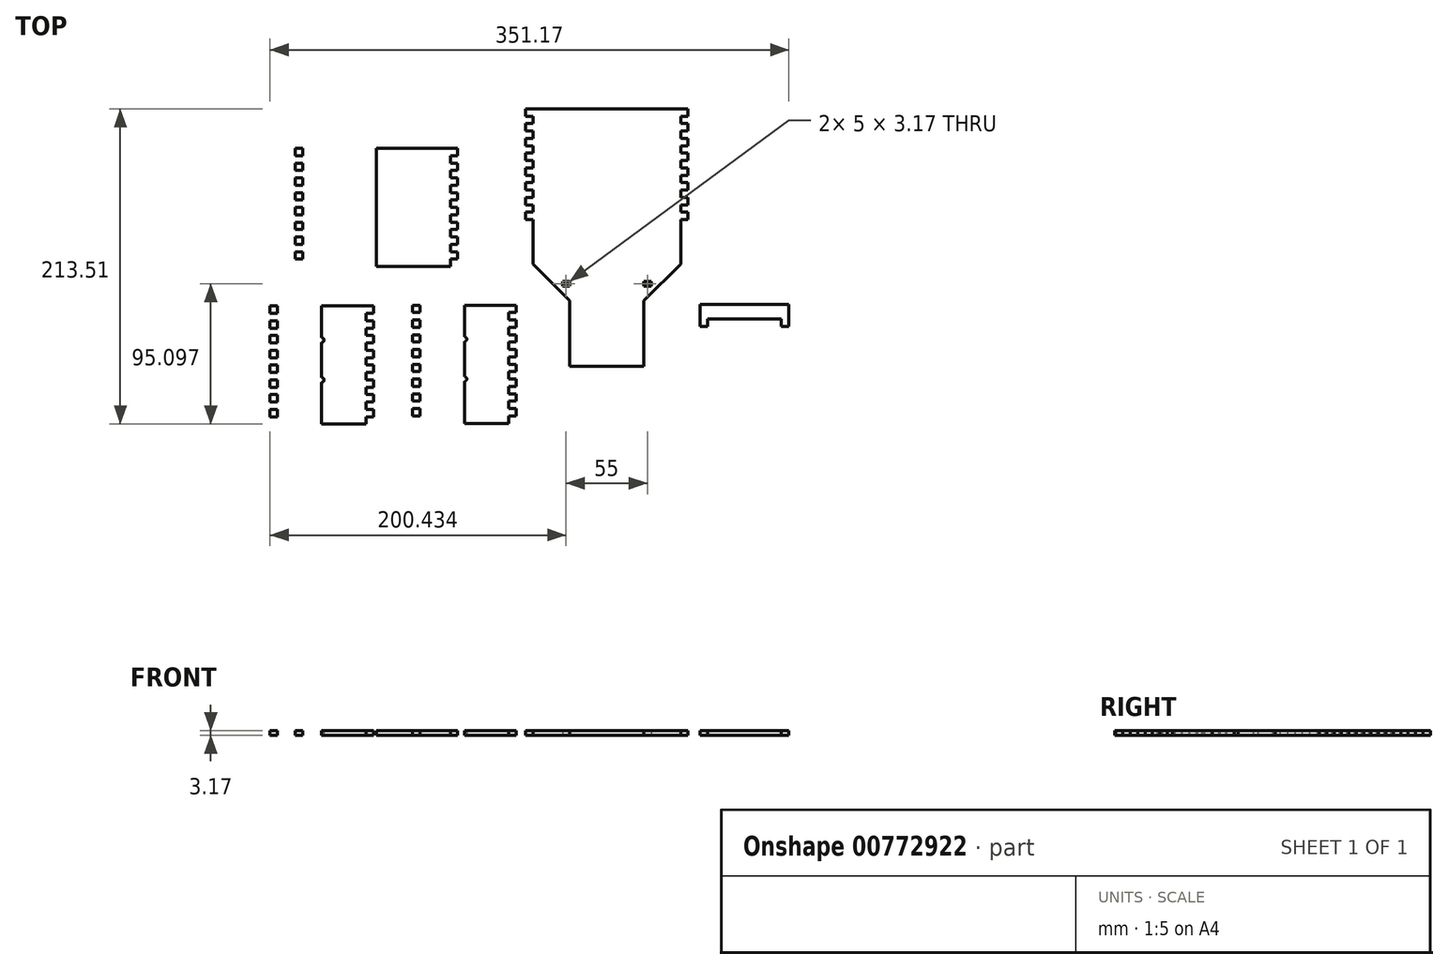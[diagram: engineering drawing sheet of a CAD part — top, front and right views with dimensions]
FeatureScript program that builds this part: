
annotation { "Feature Type Name" : "Feature", "Feature Type Description" : "" }
export const myFeature = defineFeature(function(context is Context, id is Id, definition is map)
    precondition{}
    {
        {
            var Q0;
            Q0=qCreatedBy(makeId("Top.planeOp"),FACE);
            var sketch = newSketch(context, id + "F0", { "sketchPlane" : qUnion([Q0])});
            skLineSegment(sketch, "E0", {"start": v(-34.3, 0) * mm, "end": v(-34.3, 80) * mm});
            skLineSegment(sketch, "E1.bottom", {"start": v(-34.3, 80) * mm, "end": v(-39.3, 80) * mm});
            skLineSegment(sketch, "E1.top", {"start": v(-34.3, 75) * mm, "end": v(-39.3, 75) * mm});
            skLineSegment(sketch, "E1.left", {"start": v(-34.3, 80) * mm, "end": v(-34.3, 75) * mm});
            skLineSegment(sketch, "E1.right", {"start": v(-39.3, 80) * mm, "end": v(-39.3, 75) * mm});
            skLineSegment(sketch, "E2.MirrorCS", {"start": v(-34.3, 70) * mm, "end": v(-39.3, 70) * mm});
            skLineSegment(sketch, "E3.MirrorCS", {"start": v(-34.3, 65) * mm, "end": v(-39.3, 65) * mm});
            skLineSegment(sketch, "E4.MirrorCS", {"start": v(-34.3, 60) * mm, "end": v(-39.3, 60) * mm});
            skLineSegment(sketch, "E5.MirrorCS", {"start": v(-34.3, 55) * mm, "end": v(-39.3, 55) * mm});
            skLineSegment(sketch, "E6.MirrorCS", {"start": v(-34.3, 50) * mm, "end": v(-39.3, 50) * mm});
            skLineSegment(sketch, "E7.MirrorCS", {"start": v(-34.3, 45) * mm, "end": v(-39.3, 45) * mm});
            skLineSegment(sketch, "E8.MirrorCS", {"start": v(-34.3, 40) * mm, "end": v(-39.3, 40) * mm});
            skLineSegment(sketch, "E9.MirrorCS", {"start": v(-34.3, 35) * mm, "end": v(-39.3, 35) * mm});
            skLineSegment(sketch, "E10.MirrorCS", {"start": v(-34.3, 30) * mm, "end": v(-39.3, 30) * mm});
            skLineSegment(sketch, "E11.MirrorCS", {"start": v(-34.3, 25) * mm, "end": v(-39.3, 25) * mm});
            skLineSegment(sketch, "E12.MirrorCS", {"start": v(-34.3, 20) * mm, "end": v(-39.3, 20) * mm});
            skLineSegment(sketch, "E13.MirrorCS", {"start": v(-34.3, 15) * mm, "end": v(-39.3, 15) * mm});
            skLineSegment(sketch, "E14.MirrorCS", {"start": v(-34.3, 10) * mm, "end": v(-39.3, 10) * mm});
            skLineSegment(sketch, "E15.MirrorCS", {"start": v(-34.3, 5) * mm, "end": v(-39.3, 5) * mm});
            skLineSegment(sketch, "E16", {"start": v(-34.3, 80) * mm, "end": v(15.7, 80) * mm});
            skLineSegment(sketch, "E17", {"start": v(15.7, 80) * mm, "end": v(15.7, 0) * mm});
            skLineSegment(sketch, "E18", {"start": v(15.7, 0) * mm, "end": v(-34.3, 0) * mm});
            skLineSegment(sketch, "E19", {"start": v(-39.3, 70) * mm, "end": v(-39.3, 65) * mm});
            skLineSegment(sketch, "E20", {"start": v(-39.3, 60) * mm, "end": v(-39.3, 55) * mm});
            skLineSegment(sketch, "E21", {"start": v(-39.3, 50) * mm, "end": v(-39.3, 45) * mm});
            skLineSegment(sketch, "E22", {"start": v(-39.3, 40) * mm, "end": v(-39.3, 35) * mm});
            skLineSegment(sketch, "E23", {"start": v(-39.3, 30) * mm, "end": v(-39.3, 25) * mm});
            skLineSegment(sketch, "E24", {"start": v(-39.3, 20) * mm, "end": v(-39.3, 15) * mm});
            skLineSegment(sketch, "E25", {"start": v(-39.3, 10) * mm, "end": v(-39.3, 5) * mm});
            skLineSegment(sketch, "E26.MirrorCS", {"start": v(65.7, 80) * mm, "end": v(65.7, 75) * mm});
            skLineSegment(sketch, "E27.MirrorCS", {"start": v(65.7, 45) * mm, "end": v(70.7, 45) * mm});
            skLineSegment(sketch, "E28.MirrorCS", {"start": v(65.7, 60) * mm, "end": v(70.7, 60) * mm});
            skLineSegment(sketch, "E29.MirrorCS", {"start": v(65.7, 0) * mm, "end": v(65.7, 80) * mm});
            skLineSegment(sketch, "E30.MirrorCS", {"start": v(70.7, 40) * mm, "end": v(70.7, 35) * mm});
            skLineSegment(sketch, "E31.MirrorCS", {"start": v(65.7, 80) * mm, "end": v(70.7, 80) * mm});
            skLineSegment(sketch, "E32.MirrorCS", {"start": v(65.7, 65) * mm, "end": v(70.7, 65) * mm});
            skLineSegment(sketch, "E33.MirrorCS", {"start": v(65.7, 5) * mm, "end": v(70.7, 5) * mm});
            skLineSegment(sketch, "E34.MirrorCS", {"start": v(65.7, 40) * mm, "end": v(70.7, 40) * mm});
            skLineSegment(sketch, "E35.MirrorCS", {"start": v(65.7, 50) * mm, "end": v(70.7, 50) * mm});
            skLineSegment(sketch, "E36.MirrorCS", {"start": v(70.7, 80) * mm, "end": v(70.7, 75) * mm});
            skLineSegment(sketch, "E37.MirrorCS", {"start": v(65.7, 70) * mm, "end": v(70.7, 70) * mm});
            skLineSegment(sketch, "E38.MirrorCS", {"start": v(70.7, 10) * mm, "end": v(70.7, 5) * mm});
            skLineSegment(sketch, "E39.MirrorCS", {"start": v(65.7, 35) * mm, "end": v(70.7, 35) * mm});
            skLineSegment(sketch, "E40.MirrorCS", {"start": v(65.7, 10) * mm, "end": v(70.7, 10) * mm});
            skLineSegment(sketch, "E41.MirrorCS", {"start": v(70.7, 50) * mm, "end": v(70.7, 45) * mm});
            skLineSegment(sketch, "E42.MirrorCS", {"start": v(70.7, 60) * mm, "end": v(70.7, 55) * mm});
            skLineSegment(sketch, "E43.MirrorCS", {"start": v(70.7, 30) * mm, "end": v(70.7, 25) * mm});
            skLineSegment(sketch, "E44.MirrorCS", {"start": v(70.7, 70) * mm, "end": v(70.7, 65) * mm});
            skLineSegment(sketch, "E45.MirrorCS", {"start": v(70.7, 20) * mm, "end": v(70.7, 15) * mm});
            skLineSegment(sketch, "E46.MirrorCS", {"start": v(65.7, 75) * mm, "end": v(70.7, 75) * mm});
            skLineSegment(sketch, "E47.MirrorCS", {"start": v(65.7, 55) * mm, "end": v(70.7, 55) * mm});
            skLineSegment(sketch, "E48.MirrorCS", {"start": v(65.7, 25) * mm, "end": v(70.7, 25) * mm});
            skLineSegment(sketch, "E49.MirrorCS", {"start": v(65.7, 20) * mm, "end": v(70.7, 20) * mm});
            skLineSegment(sketch, "E50.MirrorCS", {"start": v(65.7, 15) * mm, "end": v(70.7, 15) * mm});
            skLineSegment(sketch, "E51.MirrorCS", {"start": v(65.7, 30) * mm, "end": v(70.7, 30) * mm});
            skLineSegment(sketch, "E52.MirrorCS", {"start": v(15.7, 0) * mm, "end": v(65.7, 0) * mm});
            skLineSegment(sketch, "E53.MirrorCS", {"start": v(65.7, 80) * mm, "end": v(15.7, 80) * mm});
            skLineSegment(sketch, "E54", {"start": v(-34.3, 0) * mm, "end": v(-34.3, -25) * mm});
            skLineSegment(sketch, "E55", {"start": v(-34.3, -25) * mm, "end": v(-9.3, -50) * mm});
            skLineSegment(sketch, "E56", {"start": v(-9.3, -50) * mm, "end": v(15.7, -50) * mm});
            skLineSegment(sketch, "E57", {"start": v(15.7, -50) * mm, "end": v(15.7, 0) * mm});
            skLineSegment(sketch, "E58.MirrorCS", {"start": v(65.7, 0) * mm, "end": v(65.7, -25) * mm});
            skLineSegment(sketch, "E59.MirrorCS", {"start": v(65.7, -25) * mm, "end": v(40.7, -50) * mm});
            skLineSegment(sketch, "E60.MirrorCS", {"start": v(40.7, -50) * mm, "end": v(15.7, -50) * mm});
            skLineSegment(sketch, "E61", {"start": v(-9.3, -50) * mm, "end": v(3.2, -50) * mm});
            skLineSegment(sketch, "E62.bottom", {"start": v(-9.3, -40) * mm, "end": v(-14.3, -40) * mm});
            skLineSegment(sketch, "E62.top", {"start": v(-9.3, -36.83) * mm, "end": v(-14.3, -36.83) * mm});
            skLineSegment(sketch, "E62.left", {"start": v(-9.3, -40) * mm, "end": v(-9.3, -36.83) * mm});
            skLineSegment(sketch, "E62.right", {"start": v(-14.3, -40) * mm, "end": v(-14.3, -36.83) * mm});
            skLineSegment(sketch, "E63.MirrorCS", {"start": v(40.7, -36.82) * mm, "end": v(45.7, -36.82) * mm});
            skLineSegment(sketch, "E64.MirrorCS", {"start": v(40.7, -40) * mm, "end": v(45.7, -40) * mm});
            skLineSegment(sketch, "E65.MirrorCS", {"start": v(45.7, -40) * mm, "end": v(45.7, -36.83) * mm});
            skLineSegment(sketch, "E66.MirrorCS", {"start": v(40.7, -40) * mm, "end": v(40.7, -36.83) * mm});
            skLineSegment(sketch, "E67.bottom", {"start": v(78.93, -52.42) * mm, "end": v(138.93, -52.42) * mm});
            skLineSegment(sketch, "E67.top", {"start": v(78.93, -62.42) * mm, "end": v(138.93, -62.42) * mm});
            skLineSegment(sketch, "E67.left", {"start": v(78.93, -52.42) * mm, "end": v(78.93, -62.42) * mm});
            skLineSegment(sketch, "E67.right", {"start": v(138.93, -52.42) * mm, "end": v(138.93, -62.42) * mm});
            skLineSegment(sketch, "E68.bottom", {"start": v(78.93, -62.42) * mm, "end": v(83.93, -62.42) * mm});
            skLineSegment(sketch, "E68.top", {"start": v(78.93, -67.42) * mm, "end": v(83.93, -67.42) * mm});
            skLineSegment(sketch, "E68.left", {"start": v(78.93, -62.42) * mm, "end": v(78.93, -67.42) * mm});
            skLineSegment(sketch, "E68.right", {"start": v(83.93, -62.42) * mm, "end": v(83.93, -67.42) * mm});
            skLineSegment(sketch, "E69.bottom", {"start": v(138.93, -62.42) * mm, "end": v(133.93, -62.42) * mm});
            skLineSegment(sketch, "E69.top", {"start": v(138.93, -67.42) * mm, "end": v(133.93, -67.42) * mm});
            skLineSegment(sketch, "E69.left", {"start": v(138.93, -62.42) * mm, "end": v(138.93, -67.42) * mm});
            skLineSegment(sketch, "E69.right", {"start": v(133.93, -62.42) * mm, "end": v(133.93, -67.42) * mm});
            skPoint(sketch, "E70.endSnap0", {"position": v(3.2, -50) * mm});
            skLineSegment(sketch, "E71", {"start": v(6.94, -50) * mm, "end": v(-3.06, -50) * mm});
            skLineSegment(sketch, "E72.bottom", {"start": v(-9.3, -50) * mm, "end": v(40.7, -50) * mm});
            skLineSegment(sketch, "E72.top", {"start": v(-9.3, -94.45) * mm, "end": v(40.7, -94.45) * mm});
            skLineSegment(sketch, "E72.left", {"start": v(-9.3, -50) * mm, "end": v(-9.3, -94.45) * mm});
            skLineSegment(sketch, "E72.right", {"start": v(40.7, -50) * mm, "end": v(40.7, -94.45) * mm});
            skSolve(sketch);
        }
        {
            var Q0;
            Q0=qCreatedBy(makeId("Top.planeOp"),FACE);
            var sketch = newSketch(context, id + "F1", { "sketchPlane" : qUnion([Q0])});
            skLineSegment(sketch, "E73", {"start": v(-190.18, -26.72) * mm, "end": v(-190.18, 53.28) * mm});
            skLineSegment(sketch, "E74.bottom", {"start": v(-190.18, 53.28) * mm, "end": v(-195.18, 53.28) * mm});
            skLineSegment(sketch, "E74.top", {"start": v(-190.18, 48.28) * mm, "end": v(-195.18, 48.28) * mm});
            skLineSegment(sketch, "E74.left", {"start": v(-190.18, 53.28) * mm, "end": v(-190.18, 48.28) * mm});
            skLineSegment(sketch, "E74.right", {"start": v(-195.18, 53.28) * mm, "end": v(-195.18, 48.28) * mm});
            skLineSegment(sketch, "E75.MirrorCS", {"start": v(-190.18, 43.28) * mm, "end": v(-195.18, 43.28) * mm});
            skLineSegment(sketch, "E76.MirrorCS", {"start": v(-190.18, 38.28) * mm, "end": v(-195.18, 38.28) * mm});
            skLineSegment(sketch, "E77.MirrorCS", {"start": v(-190.18, 33.28) * mm, "end": v(-195.18, 33.28) * mm});
            skLineSegment(sketch, "E78.MirrorCS", {"start": v(-190.18, 28.28) * mm, "end": v(-195.18, 28.28) * mm});
            skLineSegment(sketch, "E79.MirrorCS", {"start": v(-190.18, 23.28) * mm, "end": v(-195.18, 23.28) * mm});
            skLineSegment(sketch, "E80.MirrorCS", {"start": v(-190.18, 18.28) * mm, "end": v(-195.18, 18.28) * mm});
            skLineSegment(sketch, "E81.MirrorCS", {"start": v(-190.18, 13.28) * mm, "end": v(-195.18, 13.28) * mm});
            skLineSegment(sketch, "E82.MirrorCS", {"start": v(-190.18, 8.28) * mm, "end": v(-195.18, 8.28) * mm});
            skLineSegment(sketch, "E83.MirrorCS", {"start": v(-190.18, 3.28) * mm, "end": v(-195.18, 3.28) * mm});
            skLineSegment(sketch, "E84.MirrorCS", {"start": v(-190.18, -1.72) * mm, "end": v(-195.18, -1.72) * mm});
            skLineSegment(sketch, "E85.MirrorCS", {"start": v(-190.18, -6.72) * mm, "end": v(-195.18, -6.72) * mm});
            skLineSegment(sketch, "E86.MirrorCS", {"start": v(-190.18, -11.72) * mm, "end": v(-195.18, -11.72) * mm});
            skLineSegment(sketch, "E87.MirrorCS", {"start": v(-190.18, -16.72) * mm, "end": v(-195.18, -16.72) * mm});
            skLineSegment(sketch, "E88.MirrorCS", {"start": v(-190.18, -21.72) * mm, "end": v(-195.18, -21.72) * mm});
            skLineSegment(sketch, "E89", {"start": v(-190.18, 53.28) * mm, "end": v(-140.18, 53.28) * mm});
            skLineSegment(sketch, "E90", {"start": v(-140.18, 53.28) * mm, "end": v(-140.18, -26.72) * mm});
            skLineSegment(sketch, "E91", {"start": v(-140.18, -26.72) * mm, "end": v(-190.18, -26.72) * mm});
            skLineSegment(sketch, "E92", {"start": v(-195.18, 43.28) * mm, "end": v(-195.18, 38.28) * mm});
            skLineSegment(sketch, "E93", {"start": v(-195.18, 33.28) * mm, "end": v(-195.18, 28.28) * mm});
            skLineSegment(sketch, "E94", {"start": v(-195.18, 23.28) * mm, "end": v(-195.18, 18.28) * mm});
            skLineSegment(sketch, "E95", {"start": v(-195.18, 13.28) * mm, "end": v(-195.18, 8.28) * mm});
            skLineSegment(sketch, "E96", {"start": v(-195.18, 3.28) * mm, "end": v(-195.18, -1.72) * mm});
            skLineSegment(sketch, "E97", {"start": v(-195.18, -6.72) * mm, "end": v(-195.18, -11.72) * mm});
            skLineSegment(sketch, "E98", {"start": v(-195.18, -16.72) * mm, "end": v(-195.18, -21.72) * mm});
            skLineSegment(sketch, "E99.MirrorCS", {"start": v(-90.18, 53.28) * mm, "end": v(-90.18, 48.28) * mm});
            skLineSegment(sketch, "E100.MirrorCS", {"start": v(-90.18, 18.28) * mm, "end": v(-85.18, 18.28) * mm});
            skLineSegment(sketch, "E101.MirrorCS", {"start": v(-90.18, 33.28) * mm, "end": v(-85.18, 33.28) * mm});
            skLineSegment(sketch, "E102.MirrorCS", {"start": v(-90.18, -26.72) * mm, "end": v(-90.18, 53.28) * mm});
            skLineSegment(sketch, "E103.MirrorCS", {"start": v(-85.18, 13.28) * mm, "end": v(-85.18, 8.28) * mm});
            skLineSegment(sketch, "E104.MirrorCS", {"start": v(-90.18, 53.28) * mm, "end": v(-85.18, 53.28) * mm});
            skLineSegment(sketch, "E105.MirrorCS", {"start": v(-90.18, 38.28) * mm, "end": v(-85.18, 38.28) * mm});
            skLineSegment(sketch, "E106.MirrorCS", {"start": v(-90.18, -21.72) * mm, "end": v(-85.18, -21.72) * mm});
            skLineSegment(sketch, "E107.MirrorCS", {"start": v(-90.18, 13.28) * mm, "end": v(-85.18, 13.28) * mm});
            skLineSegment(sketch, "E108.MirrorCS", {"start": v(-90.18, 23.28) * mm, "end": v(-85.18, 23.28) * mm});
            skLineSegment(sketch, "E109.MirrorCS", {"start": v(-85.18, 53.28) * mm, "end": v(-85.18, 48.28) * mm});
            skLineSegment(sketch, "E110.MirrorCS", {"start": v(-90.18, 43.28) * mm, "end": v(-85.18, 43.28) * mm});
            skLineSegment(sketch, "E111.MirrorCS", {"start": v(-85.18, -16.72) * mm, "end": v(-85.18, -21.72) * mm});
            skLineSegment(sketch, "E112.MirrorCS", {"start": v(-90.18, 8.28) * mm, "end": v(-85.18, 8.28) * mm});
            skLineSegment(sketch, "E113.MirrorCS", {"start": v(-90.18, -16.72) * mm, "end": v(-85.18, -16.72) * mm});
            skLineSegment(sketch, "E114.MirrorCS", {"start": v(-85.18, 23.28) * mm, "end": v(-85.18, 18.28) * mm});
            skLineSegment(sketch, "E115.MirrorCS", {"start": v(-85.18, 33.28) * mm, "end": v(-85.18, 28.28) * mm});
            skLineSegment(sketch, "E116.MirrorCS", {"start": v(-85.18, 3.28) * mm, "end": v(-85.18, -1.72) * mm});
            skLineSegment(sketch, "E117.MirrorCS", {"start": v(-85.18, 43.28) * mm, "end": v(-85.18, 38.28) * mm});
            skLineSegment(sketch, "E118.MirrorCS", {"start": v(-85.18, -6.72) * mm, "end": v(-85.18, -11.72) * mm});
            skLineSegment(sketch, "E119.MirrorCS", {"start": v(-90.18, 48.28) * mm, "end": v(-85.18, 48.28) * mm});
            skLineSegment(sketch, "E120.MirrorCS", {"start": v(-90.18, 28.28) * mm, "end": v(-85.18, 28.28) * mm});
            skLineSegment(sketch, "E121.MirrorCS", {"start": v(-90.18, -1.72) * mm, "end": v(-85.18, -1.72) * mm});
            skLineSegment(sketch, "E122.MirrorCS", {"start": v(-90.18, -6.72) * mm, "end": v(-85.18, -6.72) * mm});
            skLineSegment(sketch, "E123.MirrorCS", {"start": v(-90.18, -11.72) * mm, "end": v(-85.18, -11.72) * mm});
            skLineSegment(sketch, "E124.MirrorCS", {"start": v(-90.18, 3.28) * mm, "end": v(-85.18, 3.28) * mm});
            skLineSegment(sketch, "E125.MirrorCS", {"start": v(-140.18, -26.72) * mm, "end": v(-90.18, -26.72) * mm});
            skLineSegment(sketch, "E126.MirrorCS", {"start": v(-90.18, 53.28) * mm, "end": v(-140.18, 53.28) * mm});
            skLineSegment(sketch, "E127", {"start": v(-207.24, -133.51) * mm, "end": v(-207.24, -53.51) * mm});
            skLineSegment(sketch, "E128.bottom", {"start": v(-207.24, -53.51) * mm, "end": v(-212.24, -53.51) * mm});
            skLineSegment(sketch, "E128.top", {"start": v(-207.24, -58.51) * mm, "end": v(-212.24, -58.51) * mm});
            skLineSegment(sketch, "E128.left", {"start": v(-207.24, -53.51) * mm, "end": v(-207.24, -58.51) * mm});
            skLineSegment(sketch, "E128.right", {"start": v(-212.24, -53.51) * mm, "end": v(-212.24, -58.51) * mm});
            skLineSegment(sketch, "E129.MirrorCS", {"start": v(-207.24, -63.51) * mm, "end": v(-212.24, -63.51) * mm});
            skLineSegment(sketch, "E130.MirrorCS", {"start": v(-207.24, -68.51) * mm, "end": v(-212.24, -68.51) * mm});
            skLineSegment(sketch, "E131.MirrorCS", {"start": v(-207.24, -73.51) * mm, "end": v(-212.24, -73.51) * mm});
            skLineSegment(sketch, "E132.MirrorCS", {"start": v(-207.24, -78.51) * mm, "end": v(-212.24, -78.51) * mm});
            skLineSegment(sketch, "E133.MirrorCS", {"start": v(-207.24, -83.51) * mm, "end": v(-212.24, -83.51) * mm});
            skLineSegment(sketch, "E134.MirrorCS", {"start": v(-207.24, -88.51) * mm, "end": v(-212.24, -88.51) * mm});
            skLineSegment(sketch, "E135.MirrorCS", {"start": v(-207.24, -93.51) * mm, "end": v(-212.24, -93.51) * mm});
            skLineSegment(sketch, "E136.MirrorCS", {"start": v(-207.24, -98.51) * mm, "end": v(-212.24, -98.51) * mm});
            skLineSegment(sketch, "E137.MirrorCS", {"start": v(-207.24, -103.51) * mm, "end": v(-212.24, -103.51) * mm});
            skLineSegment(sketch, "E138.MirrorCS", {"start": v(-207.24, -108.51) * mm, "end": v(-212.24, -108.51) * mm});
            skLineSegment(sketch, "E139.MirrorCS", {"start": v(-207.24, -113.51) * mm, "end": v(-212.24, -113.51) * mm});
            skLineSegment(sketch, "E140.MirrorCS", {"start": v(-207.24, -118.51) * mm, "end": v(-212.24, -118.51) * mm});
            skLineSegment(sketch, "E141.MirrorCS", {"start": v(-207.24, -123.51) * mm, "end": v(-212.24, -123.51) * mm});
            skLineSegment(sketch, "E142.MirrorCS", {"start": v(-207.24, -128.51) * mm, "end": v(-212.24, -128.51) * mm});
            skLineSegment(sketch, "E143", {"start": v(-212.24, -63.51) * mm, "end": v(-212.24, -68.51) * mm});
            skLineSegment(sketch, "E144", {"start": v(-212.24, -73.51) * mm, "end": v(-212.24, -78.51) * mm});
            skLineSegment(sketch, "E145", {"start": v(-212.24, -83.51) * mm, "end": v(-212.24, -88.51) * mm});
            skLineSegment(sketch, "E146", {"start": v(-212.24, -93.51) * mm, "end": v(-212.24, -98.51) * mm});
            skLineSegment(sketch, "E147", {"start": v(-212.24, -103.51) * mm, "end": v(-212.24, -108.51) * mm});
            skLineSegment(sketch, "E148", {"start": v(-212.24, -113.51) * mm, "end": v(-212.24, -118.51) * mm});
            skLineSegment(sketch, "E149", {"start": v(-212.24, -123.51) * mm, "end": v(-212.24, -128.51) * mm});
            skLineSegment(sketch, "E150", {"start": v(-207.24, -53.51) * mm, "end": v(-177.24, -53.51) * mm});
            skLineSegment(sketch, "E151", {"start": v(-177.24, -133.51) * mm, "end": v(-207.24, -133.51) * mm});
            skLineSegment(sketch, "E152", {"start": v(-177.24, -53.51) * mm, "end": v(-177.24, -133.51) * mm});
            skLineSegment(sketch, "E153", {"start": v(-177.24, -53.51) * mm, "end": v(-177.24, -76.51) * mm});
            skCircle(sketch, "E154", {"center": v(-177.24, -76.51) * mm, "radius": 1.59 * mm});
            skLineSegment(sketch, "E155", {"start": v(-177.24, -76.51) * mm, "end": v(-177.24, -103.51) * mm});
            skCircle(sketch, "E156", {"center": v(-177.24, -103.51) * mm, "radius": 1.59 * mm});
            skLineSegment(sketch, "E157.MirrorCS", {"start": v(-142.24, -73.51) * mm, "end": v(-142.24, -78.51) * mm});
            skLineSegment(sketch, "E158.MirrorCS", {"start": v(-142.24, -63.51) * mm, "end": v(-142.24, -68.51) * mm});
            skLineSegment(sketch, "E159.MirrorCS", {"start": v(-147.24, -53.51) * mm, "end": v(-147.24, -58.51) * mm});
            skLineSegment(sketch, "E160.MirrorCS", {"start": v(-142.24, -83.51) * mm, "end": v(-142.24, -88.51) * mm});
            skLineSegment(sketch, "E161.MirrorCS", {"start": v(-142.24, -93.51) * mm, "end": v(-142.24, -98.51) * mm});
            skLineSegment(sketch, "E162.MirrorCS", {"start": v(-142.24, -103.51) * mm, "end": v(-142.24, -108.51) * mm});
            skLineSegment(sketch, "E163.MirrorCS", {"start": v(-147.24, -53.51) * mm, "end": v(-142.24, -53.51) * mm});
            skLineSegment(sketch, "E164.MirrorCS", {"start": v(-142.24, -123.51) * mm, "end": v(-142.24, -128.51) * mm});
            skLineSegment(sketch, "E165.MirrorCS", {"start": v(-142.24, -113.51) * mm, "end": v(-142.24, -118.51) * mm});
            skLineSegment(sketch, "E166.MirrorCS", {"start": v(-147.24, -58.51) * mm, "end": v(-142.24, -58.51) * mm});
            skLineSegment(sketch, "E167.MirrorCS", {"start": v(-142.24, -53.51) * mm, "end": v(-142.24, -58.51) * mm});
            skLineSegment(sketch, "E168.MirrorCS", {"start": v(-147.24, -63.51) * mm, "end": v(-142.24, -63.51) * mm});
            skLineSegment(sketch, "E169.MirrorCS", {"start": v(-147.24, -68.51) * mm, "end": v(-142.24, -68.51) * mm});
            skLineSegment(sketch, "E170.MirrorCS", {"start": v(-147.24, -73.51) * mm, "end": v(-142.24, -73.51) * mm});
            skLineSegment(sketch, "E171.MirrorCS", {"start": v(-147.24, -78.51) * mm, "end": v(-142.24, -78.51) * mm});
            skLineSegment(sketch, "E172.MirrorCS", {"start": v(-147.24, -123.51) * mm, "end": v(-142.24, -123.51) * mm});
            skLineSegment(sketch, "E173.MirrorCS", {"start": v(-147.24, -88.51) * mm, "end": v(-142.24, -88.51) * mm});
            skLineSegment(sketch, "E174.MirrorCS", {"start": v(-147.24, -83.51) * mm, "end": v(-142.24, -83.51) * mm});
            skLineSegment(sketch, "E175.MirrorCS", {"start": v(-147.24, -98.51) * mm, "end": v(-142.24, -98.51) * mm});
            skLineSegment(sketch, "E176.MirrorCS", {"start": v(-147.24, -93.51) * mm, "end": v(-142.24, -93.51) * mm});
            skLineSegment(sketch, "E177.MirrorCS", {"start": v(-147.24, -103.51) * mm, "end": v(-142.24, -103.51) * mm});
            skLineSegment(sketch, "E178.MirrorCS", {"start": v(-147.24, -128.51) * mm, "end": v(-142.24, -128.51) * mm});
            skLineSegment(sketch, "E179.MirrorCS", {"start": v(-147.24, -108.51) * mm, "end": v(-142.24, -108.51) * mm});
            skLineSegment(sketch, "E180.MirrorCS", {"start": v(-147.24, -113.51) * mm, "end": v(-142.24, -113.51) * mm});
            skLineSegment(sketch, "E181.MirrorCS", {"start": v(-147.24, -118.51) * mm, "end": v(-142.24, -118.51) * mm});
            skLineSegment(sketch, "E182.MirrorCS", {"start": v(-147.24, -133.51) * mm, "end": v(-147.24, -53.51) * mm});
            skLineSegment(sketch, "E183.MirrorCS", {"start": v(-177.24, -133.51) * mm, "end": v(-147.24, -133.51) * mm});
            skLineSegment(sketch, "E184.MirrorCS", {"start": v(-147.24, -53.51) * mm, "end": v(-177.24, -53.51) * mm});
            skLineSegment(sketch, "E185", {"start": v(-110.65, -132.98) * mm, "end": v(-110.65, -52.98) * mm});
            skLineSegment(sketch, "E186.bottom", {"start": v(-110.65, -52.98) * mm, "end": v(-115.65, -52.98) * mm});
            skLineSegment(sketch, "E186.top", {"start": v(-110.65, -57.98) * mm, "end": v(-115.65, -57.98) * mm});
            skLineSegment(sketch, "E186.left", {"start": v(-110.65, -52.98) * mm, "end": v(-110.65, -57.98) * mm});
            skLineSegment(sketch, "E186.right", {"start": v(-115.65, -52.98) * mm, "end": v(-115.65, -57.98) * mm});
            skLineSegment(sketch, "E187.MirrorCS", {"start": v(-110.65, -62.98) * mm, "end": v(-115.65, -62.98) * mm});
            skLineSegment(sketch, "E188.MirrorCS", {"start": v(-110.65, -67.98) * mm, "end": v(-115.65, -67.98) * mm});
            skLineSegment(sketch, "E189.MirrorCS", {"start": v(-110.65, -72.98) * mm, "end": v(-115.65, -72.98) * mm});
            skLineSegment(sketch, "E190.MirrorCS", {"start": v(-110.65, -77.98) * mm, "end": v(-115.65, -77.98) * mm});
            skLineSegment(sketch, "E191.MirrorCS", {"start": v(-110.65, -82.98) * mm, "end": v(-115.65, -82.98) * mm});
            skLineSegment(sketch, "E192.MirrorCS", {"start": v(-110.65, -87.98) * mm, "end": v(-115.65, -87.98) * mm});
            skLineSegment(sketch, "E193.MirrorCS", {"start": v(-110.65, -92.98) * mm, "end": v(-115.65, -92.98) * mm});
            skLineSegment(sketch, "E194.MirrorCS", {"start": v(-110.65, -97.98) * mm, "end": v(-115.65, -97.98) * mm});
            skLineSegment(sketch, "E195.MirrorCS", {"start": v(-110.65, -102.98) * mm, "end": v(-115.65, -102.98) * mm});
            skLineSegment(sketch, "E196.MirrorCS", {"start": v(-110.65, -107.98) * mm, "end": v(-115.65, -107.98) * mm});
            skLineSegment(sketch, "E197.MirrorCS", {"start": v(-110.65, -112.98) * mm, "end": v(-115.65, -112.98) * mm});
            skLineSegment(sketch, "E198.MirrorCS", {"start": v(-110.65, -117.98) * mm, "end": v(-115.65, -117.98) * mm});
            skLineSegment(sketch, "E199.MirrorCS", {"start": v(-110.65, -122.98) * mm, "end": v(-115.65, -122.98) * mm});
            skLineSegment(sketch, "E200.MirrorCS", {"start": v(-110.65, -127.98) * mm, "end": v(-115.65, -127.98) * mm});
            skLineSegment(sketch, "E201", {"start": v(-115.65, -62.98) * mm, "end": v(-115.65, -67.98) * mm});
            skLineSegment(sketch, "E202", {"start": v(-115.65, -72.98) * mm, "end": v(-115.65, -77.98) * mm});
            skLineSegment(sketch, "E203", {"start": v(-115.65, -82.98) * mm, "end": v(-115.65, -87.98) * mm});
            skLineSegment(sketch, "E204", {"start": v(-115.65, -92.98) * mm, "end": v(-115.65, -97.98) * mm});
            skLineSegment(sketch, "E205", {"start": v(-115.65, -102.98) * mm, "end": v(-115.65, -107.98) * mm});
            skLineSegment(sketch, "E206", {"start": v(-115.65, -112.98) * mm, "end": v(-115.65, -117.98) * mm});
            skLineSegment(sketch, "E207", {"start": v(-115.65, -122.98) * mm, "end": v(-115.65, -127.98) * mm});
            skLineSegment(sketch, "E208", {"start": v(-110.65, -52.98) * mm, "end": v(-80.65, -52.98) * mm});
            skLineSegment(sketch, "E209", {"start": v(-80.65, -132.98) * mm, "end": v(-110.65, -132.98) * mm});
            skLineSegment(sketch, "E210", {"start": v(-80.65, -52.98) * mm, "end": v(-80.65, -132.98) * mm});
            skLineSegment(sketch, "E211", {"start": v(-80.65, -52.98) * mm, "end": v(-80.65, -75.98) * mm});
            skCircle(sketch, "E212", {"center": v(-80.65, -75.98) * mm, "radius": 1.59 * mm});
            skLineSegment(sketch, "E213", {"start": v(-80.65, -75.98) * mm, "end": v(-80.65, -102.98) * mm});
            skCircle(sketch, "E214", {"center": v(-80.65, -102.98) * mm, "radius": 1.59 * mm});
            skLineSegment(sketch, "E215.MirrorCS", {"start": v(-45.65, -72.98) * mm, "end": v(-45.65, -77.98) * mm});
            skLineSegment(sketch, "E216.MirrorCS", {"start": v(-45.65, -62.98) * mm, "end": v(-45.65, -67.98) * mm});
            skLineSegment(sketch, "E217.MirrorCS", {"start": v(-50.65, -52.98) * mm, "end": v(-50.65, -57.98) * mm});
            skLineSegment(sketch, "E218.MirrorCS", {"start": v(-45.65, -82.98) * mm, "end": v(-45.65, -87.98) * mm});
            skLineSegment(sketch, "E219.MirrorCS", {"start": v(-45.65, -92.98) * mm, "end": v(-45.65, -97.98) * mm});
            skLineSegment(sketch, "E220.MirrorCS", {"start": v(-45.65, -102.98) * mm, "end": v(-45.65, -107.98) * mm});
            skLineSegment(sketch, "E221.MirrorCS", {"start": v(-50.65, -52.98) * mm, "end": v(-45.65, -52.98) * mm});
            skLineSegment(sketch, "E222.MirrorCS", {"start": v(-45.65, -122.98) * mm, "end": v(-45.65, -127.98) * mm});
            skLineSegment(sketch, "E223.MirrorCS", {"start": v(-45.65, -112.98) * mm, "end": v(-45.65, -117.98) * mm});
            skLineSegment(sketch, "E224.MirrorCS", {"start": v(-50.65, -57.98) * mm, "end": v(-45.65, -57.98) * mm});
            skLineSegment(sketch, "E225.MirrorCS", {"start": v(-45.65, -52.98) * mm, "end": v(-45.65, -57.98) * mm});
            skLineSegment(sketch, "E226.MirrorCS", {"start": v(-50.65, -62.98) * mm, "end": v(-45.65, -62.98) * mm});
            skLineSegment(sketch, "E227.MirrorCS", {"start": v(-50.65, -67.98) * mm, "end": v(-45.65, -67.98) * mm});
            skLineSegment(sketch, "E228.MirrorCS", {"start": v(-50.65, -72.98) * mm, "end": v(-45.65, -72.98) * mm});
            skLineSegment(sketch, "E229.MirrorCS", {"start": v(-50.65, -77.98) * mm, "end": v(-45.65, -77.98) * mm});
            skLineSegment(sketch, "E230.MirrorCS", {"start": v(-50.65, -122.98) * mm, "end": v(-45.65, -122.98) * mm});
            skLineSegment(sketch, "E231.MirrorCS", {"start": v(-50.65, -87.98) * mm, "end": v(-45.65, -87.98) * mm});
            skLineSegment(sketch, "E232.MirrorCS", {"start": v(-50.65, -82.98) * mm, "end": v(-45.65, -82.98) * mm});
            skLineSegment(sketch, "E233.MirrorCS", {"start": v(-50.65, -97.98) * mm, "end": v(-45.65, -97.98) * mm});
            skLineSegment(sketch, "E234.MirrorCS", {"start": v(-50.65, -92.98) * mm, "end": v(-45.65, -92.98) * mm});
            skLineSegment(sketch, "E235.MirrorCS", {"start": v(-50.65, -102.98) * mm, "end": v(-45.65, -102.98) * mm});
            skLineSegment(sketch, "E236.MirrorCS", {"start": v(-50.65, -127.98) * mm, "end": v(-45.65, -127.98) * mm});
            skLineSegment(sketch, "E237.MirrorCS", {"start": v(-50.65, -107.98) * mm, "end": v(-45.65, -107.98) * mm});
            skLineSegment(sketch, "E238.MirrorCS", {"start": v(-50.65, -112.98) * mm, "end": v(-45.65, -112.98) * mm});
            skLineSegment(sketch, "E239.MirrorCS", {"start": v(-50.65, -117.98) * mm, "end": v(-45.65, -117.98) * mm});
            skLineSegment(sketch, "E240.MirrorCS", {"start": v(-50.65, -132.98) * mm, "end": v(-50.65, -52.98) * mm});
            skLineSegment(sketch, "E241.MirrorCS", {"start": v(-80.65, -132.98) * mm, "end": v(-50.65, -132.98) * mm});
            skLineSegment(sketch, "E242.MirrorCS", {"start": v(-50.65, -52.98) * mm, "end": v(-80.65, -52.98) * mm});
            skSolve(sketch);
        }
        {
            var Q0;
            {var subQ0=sQuery(id+"F0.wireOp",EDGE,"E33.MirrorCS");Q0=makeQuery(id+"F0.imprint","IMPRINT",FACE,{"disambiguationData":[TD([[makeQuery(id+"F0.imprint","IMPRINT",EDGE,{"derivedFrom":subQ0}),1.0]])]});}
            var Q1;
            Q1=makeQuery(id+"F0.imprint","IMPRINT",FACE,{"disambiguationData":[TD([[makeQuery(id+"F0.imprint","IMPRINT",EDGE,{"derivedFrom":sQuery(id+"F0.wireOp",EDGE,"E45.MirrorCS")}),-1.0]])]});
            var Q2;
            Q2=makeQuery(id+"F0.imprint","IMPRINT",FACE,{"disambiguationData":[TD([[makeQuery(id+"F0.imprint","IMPRINT",EDGE,{"derivedFrom":sQuery(id+"F0.wireOp",EDGE,"E43.MirrorCS")}),-1.0]])]});
            var Q3;
            Q3=makeQuery(id+"F0.imprint","IMPRINT",FACE,{"disambiguationData":[TD([[makeQuery(id+"F0.imprint","IMPRINT",EDGE,{"derivedFrom":sQuery(id+"F0.wireOp",EDGE,"E30.MirrorCS")}),-1.0]])]});
            var Q4;
            {var subQ0=sQuery(id+"F0.wireOp",EDGE,"E27.MirrorCS");Q4=makeQuery(id+"F0.imprint","IMPRINT",FACE,{"disambiguationData":[TD([[makeQuery(id+"F0.imprint","IMPRINT",EDGE,{"derivedFrom":subQ0}),1.0]])]});}
            var Q5;
            {var subQ0=sQuery(id+"F0.wireOp",EDGE,"E28.MirrorCS");Q5=makeQuery(id+"F0.imprint","IMPRINT",FACE,{"disambiguationData":[TD([[makeQuery(id+"F0.imprint","IMPRINT",EDGE,{"derivedFrom":subQ0}),-1.0]])]});}
            var Q6;
            {var subQ0=sQuery(id+"F0.wireOp",EDGE,"E32.MirrorCS");Q6=makeQuery(id+"F0.imprint","IMPRINT",FACE,{"disambiguationData":[TD([[makeQuery(id+"F0.imprint","IMPRINT",EDGE,{"derivedFrom":subQ0}),1.0]])]});}
            var Q7;
            Q7=makeQuery(id+"F0.imprint","IMPRINT",FACE,{"disambiguationData":[TD([[makeQuery(id+"F0.imprint","IMPRINT",EDGE,{"derivedFrom":sQuery(id+"F0.wireOp",EDGE,"E26.MirrorCS")}),1.0]])]});
            var Q8;
            Q8=makeQuery(id+"F0.imprint","IMPRINT",FACE,{"disambiguationData":[TD([[makeQuery(id+"F0.imprint","IMPRINT",EDGE,{"derivedFrom":sQuery(id+"F0.wireOp",EDGE,"E17")}),1.0]])]});
            var Q9;
            {var subQ16=sQuery(id+"F0.wireOp",EDGE,"E16");Q9=makeQuery(id+"F0.imprint","IMPRINT",FACE,{"disambiguationData":[TD([[makeQuery(id+"F0.imprint","IMPRINT",EDGE,{"derivedFrom":subQ16}),-1.0]])]});}
            var Q10;
            Q10=makeQuery(id+"F0.imprint","IMPRINT",FACE,{"disambiguationData":[TD([[makeQuery(id+"F0.imprint","IMPRINT",EDGE,{"derivedFrom":sQuery(id+"F0.wireOp",EDGE,"E18")}),1.0]])]});
            var Q11;
            Q11=makeQuery(id+"F0.imprint","IMPRINT",FACE,{"disambiguationData":[TD([[makeQuery(id+"F0.imprint","IMPRINT",EDGE,{"derivedFrom":sQuery(id+"F0.wireOp",EDGE,"E52.MirrorCS")}),-1.0]])]});
            var Q12;
            {var subQ2=sQuery(id+"F0.wireOp",EDGE,"E14.MirrorCS");Q12=makeQuery(id+"F0.imprint","IMPRINT",FACE,{"disambiguationData":[TD([[makeQuery(id+"F0.imprint","IMPRINT",EDGE,{"derivedFrom":subQ2}),1.0]])]});}
            var Q13;
            {var subQ0=sQuery(id+"F0.wireOp",EDGE,"E12.MirrorCS");Q13=makeQuery(id+"F0.imprint","IMPRINT",FACE,{"disambiguationData":[TD([[makeQuery(id+"F0.imprint","IMPRINT",EDGE,{"derivedFrom":subQ0}),1.0]])]});}
            var Q14;
            {var subQ0=sQuery(id+"F0.wireOp",EDGE,"E10.MirrorCS");Q14=makeQuery(id+"F0.imprint","IMPRINT",FACE,{"disambiguationData":[TD([[makeQuery(id+"F0.imprint","IMPRINT",EDGE,{"derivedFrom":subQ0}),1.0]])]});}
            var Q15;
            {var subQ0=sQuery(id+"F0.wireOp",EDGE,"E8.MirrorCS");Q15=makeQuery(id+"F0.imprint","IMPRINT",FACE,{"disambiguationData":[TD([[makeQuery(id+"F0.imprint","IMPRINT",EDGE,{"derivedFrom":subQ0}),1.0]])]});}
            var Q16;
            {var subQ0=sQuery(id+"F0.wireOp",EDGE,"E6.MirrorCS");Q16=makeQuery(id+"F0.imprint","IMPRINT",FACE,{"disambiguationData":[TD([[makeQuery(id+"F0.imprint","IMPRINT",EDGE,{"derivedFrom":subQ0}),1.0]])]});}
            var Q17;
            {var subQ2=sQuery(id+"F0.wireOp",EDGE,"E4.MirrorCS");Q17=makeQuery(id+"F0.imprint","IMPRINT",FACE,{"disambiguationData":[TD([[makeQuery(id+"F0.imprint","IMPRINT",EDGE,{"derivedFrom":subQ2}),1.0]])]});}
            var Q18;
            {var subQ0=sQuery(id+"F0.wireOp",EDGE,"E2.MirrorCS");Q18=makeQuery(id+"F0.imprint","IMPRINT",FACE,{"disambiguationData":[TD([[makeQuery(id+"F0.imprint","IMPRINT",EDGE,{"derivedFrom":subQ0}),1.0]])]});}
            var Q19;
            {var subQ0=sQuery(id+"F0.wireOp",EDGE,"E1.bottom");Q19=makeQuery(id+"F0.imprint","IMPRINT",FACE,{"disambiguationData":[TD([[makeQuery(id+"F0.imprint","IMPRINT",EDGE,{"derivedFrom":subQ0}),1.0]])]});}
            var Q20;
            Q20=makeQuery(id+"F0.imprint","IMPRINT",FACE,{"disambiguationData":[TD([[makeQuery(id+"F0.imprint","IMPRINT",EDGE,{"derivedFrom":sQuery(id+"F0.wireOp",EDGE,"E67.bottom")}),-1.0]])]});
            var Q21;
            Q21=makeQuery(id+"F0.imprint","IMPRINT",FACE,{"disambiguationData":[TD([[makeQuery(id+"F0.imprint","IMPRINT",EDGE,{"derivedFrom":sQuery(id+"F0.wireOp",EDGE,"E68.top")}),1.0]])]});
            var Q22;
            Q22=makeQuery(id+"F0.imprint","IMPRINT",FACE,{"disambiguationData":[TD([[makeQuery(id+"F0.imprint","IMPRINT",EDGE,{"derivedFrom":sQuery(id+"F0.wireOp",EDGE,"E69.top")}),-1.0]])]});
            var Q23;
            {var subQ8=sQuery(id+"F1.wireOp",EDGE,"E128.left");Q23=makeQuery(id+"F1.imprint","IMPRINT",FACE,{"disambiguationData":[TD([[makeQuery(id+"F1.imprint","IMPRINT",EDGE,{"derivedFrom":subQ8}),1.0]])]});}
            var Q24;
            {var subQ0=sQuery(id+"F1.wireOp",EDGE,"E141.MirrorCS");Q24=makeQuery(id+"F1.imprint","IMPRINT",FACE,{"disambiguationData":[TD([[makeQuery(id+"F1.imprint","IMPRINT",EDGE,{"derivedFrom":subQ0}),1.0]])]});}
            var Q25;
            {var subQ0=sQuery(id+"F1.wireOp",EDGE,"E139.MirrorCS");Q25=makeQuery(id+"F1.imprint","IMPRINT",FACE,{"disambiguationData":[TD([[makeQuery(id+"F1.imprint","IMPRINT",EDGE,{"derivedFrom":subQ0}),1.0]])]});}
            var Q26;
            {var subQ0=sQuery(id+"F1.wireOp",EDGE,"E137.MirrorCS");Q26=makeQuery(id+"F1.imprint","IMPRINT",FACE,{"disambiguationData":[TD([[makeQuery(id+"F1.imprint","IMPRINT",EDGE,{"derivedFrom":subQ0}),1.0]])]});}
            var Q27;
            {var subQ0=sQuery(id+"F1.wireOp",EDGE,"E135.MirrorCS");Q27=makeQuery(id+"F1.imprint","IMPRINT",FACE,{"disambiguationData":[TD([[makeQuery(id+"F1.imprint","IMPRINT",EDGE,{"derivedFrom":subQ0}),1.0]])]});}
            var Q28;
            {var subQ0=sQuery(id+"F1.wireOp",EDGE,"E133.MirrorCS");Q28=makeQuery(id+"F1.imprint","IMPRINT",FACE,{"disambiguationData":[TD([[makeQuery(id+"F1.imprint","IMPRINT",EDGE,{"derivedFrom":subQ0}),1.0]])]});}
            var Q29;
            {var subQ0=sQuery(id+"F1.wireOp",EDGE,"E131.MirrorCS");Q29=makeQuery(id+"F1.imprint","IMPRINT",FACE,{"disambiguationData":[TD([[makeQuery(id+"F1.imprint","IMPRINT",EDGE,{"derivedFrom":subQ0}),1.0]])]});}
            var Q30;
            {var subQ0=sQuery(id+"F1.wireOp",EDGE,"E129.MirrorCS");Q30=makeQuery(id+"F1.imprint","IMPRINT",FACE,{"disambiguationData":[TD([[makeQuery(id+"F1.imprint","IMPRINT",EDGE,{"derivedFrom":subQ0}),1.0]])]});}
            var Q31;
            Q31=makeQuery(id+"F1.imprint","IMPRINT",FACE,{"disambiguationData":[TD([[makeQuery(id+"F1.imprint","IMPRINT",EDGE,{"derivedFrom":sQuery(id+"F1.wireOp",EDGE,"E128.bottom")}),1.0]])]});
            var Q32;
            {var subQ16=sQuery(id+"F1.wireOp",EDGE,"E74.left");Q32=makeQuery(id+"F1.imprint","IMPRINT",FACE,{"disambiguationData":[TD([[makeQuery(id+"F1.imprint","IMPRINT",EDGE,{"derivedFrom":subQ16}),1.0]])]});}
            var Q33;
            Q33=makeQuery(id+"F1.imprint","IMPRINT",FACE,{"disambiguationData":[TD([[makeQuery(id+"F1.imprint","IMPRINT",EDGE,{"derivedFrom":sQuery(id+"F1.wireOp",EDGE,"E90")}),1.0]])]});
            var Q34;
            Q34=makeQuery(id+"F1.imprint","IMPRINT",FACE,{"disambiguationData":[TD([[makeQuery(id+"F1.imprint","IMPRINT",EDGE,{"derivedFrom":sQuery(id+"F1.wireOp",EDGE,"E109.MirrorCS")}),-1.0]])]});
            var Q35;
            Q35=makeQuery(id+"F1.imprint","IMPRINT",FACE,{"disambiguationData":[TD([[makeQuery(id+"F1.imprint","IMPRINT",EDGE,{"derivedFrom":sQuery(id+"F1.wireOp",EDGE,"E117.MirrorCS")}),-1.0]])]});
            var Q36;
            Q36=makeQuery(id+"F1.imprint","IMPRINT",FACE,{"disambiguationData":[TD([[makeQuery(id+"F1.imprint","IMPRINT",EDGE,{"derivedFrom":sQuery(id+"F1.wireOp",EDGE,"E115.MirrorCS")}),-1.0]])]});
            var Q37;
            Q37=makeQuery(id+"F1.imprint","IMPRINT",FACE,{"disambiguationData":[TD([[makeQuery(id+"F1.imprint","IMPRINT",EDGE,{"derivedFrom":sQuery(id+"F1.wireOp",EDGE,"E114.MirrorCS")}),-1.0]])]});
            var Q38;
            Q38=makeQuery(id+"F1.imprint","IMPRINT",FACE,{"disambiguationData":[TD([[makeQuery(id+"F1.imprint","IMPRINT",EDGE,{"derivedFrom":sQuery(id+"F1.wireOp",EDGE,"E103.MirrorCS")}),-1.0]])]});
            var Q39;
            Q39=makeQuery(id+"F1.imprint","IMPRINT",FACE,{"disambiguationData":[TD([[makeQuery(id+"F1.imprint","IMPRINT",EDGE,{"derivedFrom":sQuery(id+"F1.wireOp",EDGE,"E116.MirrorCS")}),-1.0]])]});
            var Q40;
            Q40=makeQuery(id+"F1.imprint","IMPRINT",FACE,{"disambiguationData":[TD([[makeQuery(id+"F1.imprint","IMPRINT",EDGE,{"derivedFrom":sQuery(id+"F1.wireOp",EDGE,"E118.MirrorCS")}),-1.0]])]});
            var Q41;
            {var subQ0=sQuery(id+"F1.wireOp",EDGE,"E106.MirrorCS");Q41=makeQuery(id+"F1.imprint","IMPRINT",FACE,{"disambiguationData":[TD([[makeQuery(id+"F1.imprint","IMPRINT",EDGE,{"derivedFrom":subQ0}),1.0]])]});}
            var Q42;
            {var subQ0=sQuery(id+"F1.wireOp",EDGE,"E87.MirrorCS");Q42=makeQuery(id+"F1.imprint","IMPRINT",FACE,{"disambiguationData":[TD([[makeQuery(id+"F1.imprint","IMPRINT",EDGE,{"derivedFrom":subQ0}),1.0]])]});}
            var Q43;
            {var subQ0=sQuery(id+"F1.wireOp",EDGE,"E85.MirrorCS");Q43=makeQuery(id+"F1.imprint","IMPRINT",FACE,{"disambiguationData":[TD([[makeQuery(id+"F1.imprint","IMPRINT",EDGE,{"derivedFrom":subQ0}),1.0]])]});}
            var Q44;
            {var subQ0=sQuery(id+"F1.wireOp",EDGE,"E83.MirrorCS");Q44=makeQuery(id+"F1.imprint","IMPRINT",FACE,{"disambiguationData":[TD([[makeQuery(id+"F1.imprint","IMPRINT",EDGE,{"derivedFrom":subQ0}),1.0]])]});}
            var Q45;
            {var subQ0=sQuery(id+"F1.wireOp",EDGE,"E81.MirrorCS");Q45=makeQuery(id+"F1.imprint","IMPRINT",FACE,{"disambiguationData":[TD([[makeQuery(id+"F1.imprint","IMPRINT",EDGE,{"derivedFrom":subQ0}),1.0]])]});}
            var Q46;
            {var subQ0=sQuery(id+"F1.wireOp",EDGE,"E79.MirrorCS");Q46=makeQuery(id+"F1.imprint","IMPRINT",FACE,{"disambiguationData":[TD([[makeQuery(id+"F1.imprint","IMPRINT",EDGE,{"derivedFrom":subQ0}),1.0]])]});}
            var Q47;
            {var subQ0=sQuery(id+"F1.wireOp",EDGE,"E77.MirrorCS");Q47=makeQuery(id+"F1.imprint","IMPRINT",FACE,{"disambiguationData":[TD([[makeQuery(id+"F1.imprint","IMPRINT",EDGE,{"derivedFrom":subQ0}),1.0]])]});}
            var Q48;
            {var subQ0=sQuery(id+"F1.wireOp",EDGE,"E75.MirrorCS");Q48=makeQuery(id+"F1.imprint","IMPRINT",FACE,{"disambiguationData":[TD([[makeQuery(id+"F1.imprint","IMPRINT",EDGE,{"derivedFrom":subQ0}),1.0]])]});}
            var Q49;
            Q49=makeQuery(id+"F1.imprint","IMPRINT",FACE,{"disambiguationData":[TD([[makeQuery(id+"F1.imprint","IMPRINT",EDGE,{"derivedFrom":sQuery(id+"F1.wireOp",EDGE,"E74.bottom")}),1.0]])]});
            var Q50;
            {var subQ5=sQuery(id+"F0.wireOp",EDGE,"E60.MirrorCS");Q50=makeQuery(id+"F0.imprint","IMPRINT",FACE,{"disambiguationData":[TD([[makeQuery(id+"F0.imprint","IMPRINT",EDGE,{"derivedFrom":subQ5}),1.0]])]});}
            var Q51;
            {var subQ15=sQuery(id+"F1.wireOp",EDGE,"E183.MirrorCS");Q51=makeQuery(id+"F1.imprint","IMPRINT",FACE,{"disambiguationData":[TD([[makeQuery(id+"F1.imprint","IMPRINT",EDGE,{"derivedFrom":subQ15}),1.0]])]});}
            var Q52;
            Q52=makeQuery(id+"F1.imprint","IMPRINT",FACE,{"disambiguationData":[TD([[makeQuery(id+"F1.imprint","IMPRINT",EDGE,{"derivedFrom":sQuery(id+"F1.wireOp",EDGE,"E157.MirrorCS")}),-1.0]])]});
            var Q53;
            Q53=makeQuery(id+"F1.imprint","IMPRINT",FACE,{"disambiguationData":[TD([[makeQuery(id+"F1.imprint","IMPRINT",EDGE,{"derivedFrom":sQuery(id+"F1.wireOp",EDGE,"E160.MirrorCS")}),-1.0]])]});
            var Q54;
            {var subQ0=sQuery(id+"F1.wireOp",EDGE,"E163.MirrorCS");Q54=makeQuery(id+"F1.imprint","IMPRINT",FACE,{"disambiguationData":[TD([[makeQuery(id+"F1.imprint","IMPRINT",EDGE,{"derivedFrom":subQ0}),-1.0]])]});}
            var Q55;
            Q55=makeQuery(id+"F1.imprint","IMPRINT",FACE,{"disambiguationData":[TD([[makeQuery(id+"F1.imprint","IMPRINT",EDGE,{"derivedFrom":sQuery(id+"F1.wireOp",EDGE,"E165.MirrorCS")}),-1.0]])]});
            var Q56;
            Q56=makeQuery(id+"F1.imprint","IMPRINT",FACE,{"disambiguationData":[TD([[makeQuery(id+"F1.imprint","IMPRINT",EDGE,{"derivedFrom":sQuery(id+"F1.wireOp",EDGE,"E158.MirrorCS")}),-1.0]])]});
            var Q57;
            Q57=makeQuery(id+"F1.imprint","IMPRINT",FACE,{"disambiguationData":[TD([[makeQuery(id+"F1.imprint","IMPRINT",EDGE,{"derivedFrom":sQuery(id+"F1.wireOp",EDGE,"E161.MirrorCS")}),-1.0]])]});
            var Q58;
            Q58=makeQuery(id+"F1.imprint","IMPRINT",FACE,{"disambiguationData":[TD([[makeQuery(id+"F1.imprint","IMPRINT",EDGE,{"derivedFrom":sQuery(id+"F1.wireOp",EDGE,"E164.MirrorCS")}),-1.0]])]});
            var Q59;
            Q59=makeQuery(id+"F1.imprint","IMPRINT",FACE,{"disambiguationData":[TD([[makeQuery(id+"F1.imprint","IMPRINT",EDGE,{"derivedFrom":sQuery(id+"F1.wireOp",EDGE,"E162.MirrorCS")}),-1.0]])]});
            var Q60;
            {var subQ8=sQuery(id+"F1.wireOp",EDGE,"E186.left");Q60=makeQuery(id+"F1.imprint","IMPRINT",FACE,{"disambiguationData":[TD([[makeQuery(id+"F1.imprint","IMPRINT",EDGE,{"derivedFrom":subQ8}),1.0]])]});}
            var Q61;
            {var subQ15=sQuery(id+"F1.wireOp",EDGE,"E241.MirrorCS");Q61=makeQuery(id+"F1.imprint","IMPRINT",FACE,{"disambiguationData":[TD([[makeQuery(id+"F1.imprint","IMPRINT",EDGE,{"derivedFrom":subQ15}),1.0]])]});}
            var Q62;
            Q62=makeQuery(id+"F1.imprint","IMPRINT",FACE,{"disambiguationData":[TD([[makeQuery(id+"F1.imprint","IMPRINT",EDGE,{"derivedFrom":sQuery(id+"F1.wireOp",EDGE,"E220.MirrorCS")}),-1.0]])]});
            var Q63;
            Q63=makeQuery(id+"F1.imprint","IMPRINT",FACE,{"disambiguationData":[TD([[makeQuery(id+"F1.imprint","IMPRINT",EDGE,{"derivedFrom":sQuery(id+"F1.wireOp",EDGE,"E218.MirrorCS")}),-1.0]])]});
            var Q64;
            Q64=makeQuery(id+"F1.imprint","IMPRINT",FACE,{"disambiguationData":[TD([[makeQuery(id+"F1.imprint","IMPRINT",EDGE,{"derivedFrom":sQuery(id+"F1.wireOp",EDGE,"E215.MirrorCS")}),-1.0]])]});
            var Q65;
            Q65=makeQuery(id+"F1.imprint","IMPRINT",FACE,{"disambiguationData":[TD([[makeQuery(id+"F1.imprint","IMPRINT",EDGE,{"derivedFrom":sQuery(id+"F1.wireOp",EDGE,"E216.MirrorCS")}),-1.0]])]});
            var Q66;
            Q66=makeQuery(id+"F1.imprint","IMPRINT",FACE,{"disambiguationData":[TD([[makeQuery(id+"F1.imprint","IMPRINT",EDGE,{"derivedFrom":sQuery(id+"F1.wireOp",EDGE,"E223.MirrorCS")}),-1.0]])]});
            var Q67;
            Q67=makeQuery(id+"F1.imprint","IMPRINT",FACE,{"disambiguationData":[TD([[makeQuery(id+"F1.imprint","IMPRINT",EDGE,{"derivedFrom":sQuery(id+"F1.wireOp",EDGE,"E219.MirrorCS")}),-1.0]])]});
            var Q68;
            Q68=makeQuery(id+"F1.imprint","IMPRINT",FACE,{"disambiguationData":[TD([[makeQuery(id+"F1.imprint","IMPRINT",EDGE,{"derivedFrom":sQuery(id+"F1.wireOp",EDGE,"E222.MirrorCS")}),-1.0]])]});
            var Q69;
            {var subQ0=sQuery(id+"F1.wireOp",EDGE,"E221.MirrorCS");Q69=makeQuery(id+"F1.imprint","IMPRINT",FACE,{"disambiguationData":[TD([[makeQuery(id+"F1.imprint","IMPRINT",EDGE,{"derivedFrom":subQ0}),-1.0]])]});}
            var Q70;
            {var subQ0=sQuery(id+"F1.wireOp",EDGE,"E197.MirrorCS");Q70=makeQuery(id+"F1.imprint","IMPRINT",FACE,{"disambiguationData":[TD([[makeQuery(id+"F1.imprint","IMPRINT",EDGE,{"derivedFrom":subQ0}),1.0]])]});}
            var Q71;
            {var subQ0=sQuery(id+"F1.wireOp",EDGE,"E195.MirrorCS");Q71=makeQuery(id+"F1.imprint","IMPRINT",FACE,{"disambiguationData":[TD([[makeQuery(id+"F1.imprint","IMPRINT",EDGE,{"derivedFrom":subQ0}),1.0]])]});}
            var Q72;
            {var subQ0=sQuery(id+"F1.wireOp",EDGE,"E189.MirrorCS");Q72=makeQuery(id+"F1.imprint","IMPRINT",FACE,{"disambiguationData":[TD([[makeQuery(id+"F1.imprint","IMPRINT",EDGE,{"derivedFrom":subQ0}),1.0]])]});}
            var Q73;
            {var subQ0=sQuery(id+"F1.wireOp",EDGE,"E193.MirrorCS");Q73=makeQuery(id+"F1.imprint","IMPRINT",FACE,{"disambiguationData":[TD([[makeQuery(id+"F1.imprint","IMPRINT",EDGE,{"derivedFrom":subQ0}),1.0]])]});}
            var Q74;
            {var subQ0=sQuery(id+"F1.wireOp",EDGE,"E191.MirrorCS");Q74=makeQuery(id+"F1.imprint","IMPRINT",FACE,{"disambiguationData":[TD([[makeQuery(id+"F1.imprint","IMPRINT",EDGE,{"derivedFrom":subQ0}),1.0]])]});}
            var Q75;
            {var subQ0=sQuery(id+"F1.wireOp",EDGE,"E187.MirrorCS");Q75=makeQuery(id+"F1.imprint","IMPRINT",FACE,{"disambiguationData":[TD([[makeQuery(id+"F1.imprint","IMPRINT",EDGE,{"derivedFrom":subQ0}),1.0]])]});}
            var Q76;
            Q76=makeQuery(id+"F1.imprint","IMPRINT",FACE,{"disambiguationData":[TD([[makeQuery(id+"F1.imprint","IMPRINT",EDGE,{"derivedFrom":sQuery(id+"F1.wireOp",EDGE,"E186.bottom")}),1.0]])]});
            var Q77;
            {var subQ0=sQuery(id+"F1.wireOp",EDGE,"E199.MirrorCS");Q77=makeQuery(id+"F1.imprint","IMPRINT",FACE,{"disambiguationData":[TD([[makeQuery(id+"F1.imprint","IMPRINT",EDGE,{"derivedFrom":subQ0}),1.0]])]});}
            extrude(context, id + "F2", {"entities" : qUnion([Q0, Q1, Q2, Q3, Q4, Q5, Q6, Q7, Q8, Q9, Q10, Q11, Q12, Q13, Q14, Q15, Q16, Q17, Q18, Q19, Q20, Q21, Q22, Q23, Q24, Q25, Q26, Q27, Q28, Q29, Q30, Q31, Q32, Q33, Q34, Q35, Q36, Q37, Q38, Q39, Q40, Q41, Q42, Q43, Q44, Q45, Q46, Q47, Q48, Q49, Q50, Q51, Q52, Q53, Q54, Q55, Q56, Q57, Q58, Q59, Q60, Q61, Q62, Q63, Q64, Q65, Q66, Q67, Q68, Q69, Q70, Q71, Q72, Q73, Q74, Q75, Q76, Q77]), "depth" : 3.17 * mm, "offsetDistance" : 25 * mm});
        }
    });
